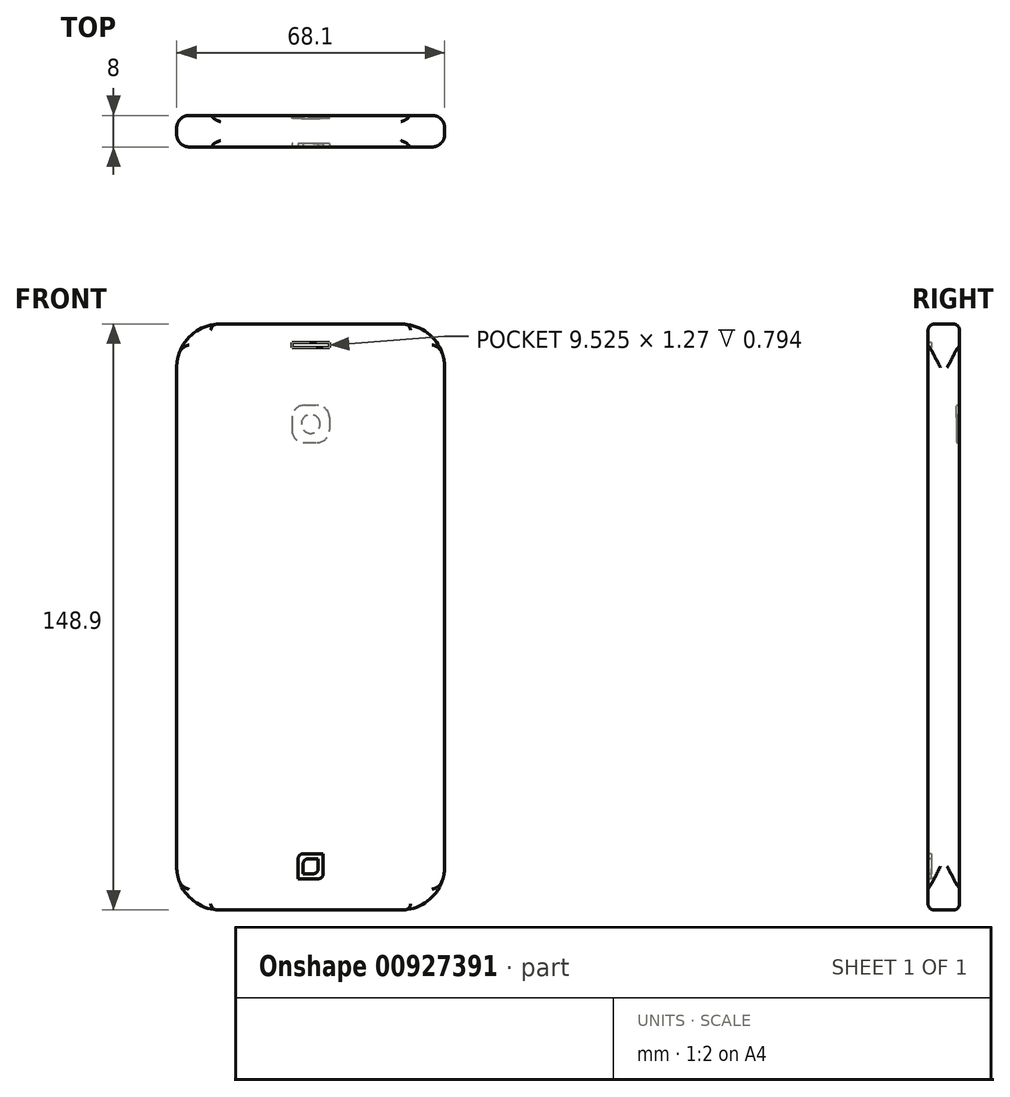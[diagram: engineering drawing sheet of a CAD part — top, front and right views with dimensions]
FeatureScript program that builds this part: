
annotation { "Feature Type Name" : "Feature", "Feature Type Description" : "" }
export const myFeature = defineFeature(function(context is Context, id is Id, definition is map)
    precondition{}
    {
        {
            var Q0;
            Q0=qCreatedBy(makeId("Front.planeOp"),FACE);
            var sketch = newSketch(context, id + "F0", { "sketchPlane" : qUnion([Q0])});
            skLineSegment(sketch, "E0.bottom", {"start": v(34.05, 74.45) * mm, "end": v(-34.05, 74.45) * mm});
            skLineSegment(sketch, "E0.top", {"start": v(34.05, -74.45) * mm, "end": v(-34.05, -74.45) * mm});
            skLineSegment(sketch, "E0.left", {"start": v(34.05, 74.45) * mm, "end": v(34.05, -74.45) * mm});
            skLineSegment(sketch, "E0.right", {"start": v(-34.05, 74.45) * mm, "end": v(-34.05, -74.45) * mm});
            skPoint(sketch, "E0.middle", {"position": v(0, 0) * mm});
            skSolve(sketch);
        }
        {
            var Q0;
            Q0 = qSketchRegion(id + "F0", true);
            extrude(context, id + "F1", {"entities" : qUnion([Q0]), "depth" : 8 * mm, "offsetDistance" : 25.4 * mm});
        }
        {
            var Q0;
            Q0=makeQuery(id+"F1.opExtrude","SWEPT_EDGE",EDGE,{"disambiguationData":[OSD([sQuery(id+"F0.wireOp",EDGE,"E0.bottom"),sQuery(id+"F0.wireOp",EDGE,"E0.left")])]});
            var Q1;
            Q1=makeQuery(id+"F1.opExtrude","SWEPT_EDGE",EDGE,{"disambiguationData":[OSD([sQuery(id+"F0.wireOp",EDGE,"E0.bottom"),sQuery(id+"F0.wireOp",EDGE,"E0.right")])]});
            var Q2;
            Q2=makeQuery(id+"F1.opExtrude","SWEPT_EDGE",EDGE,{"disambiguationData":[OSD([sQuery(id+"F0.wireOp",EDGE,"E0.top"),sQuery(id+"F0.wireOp",EDGE,"E0.right")])]});
            var Q3;
            Q3=makeQuery(id+"F1.opExtrude","SWEPT_EDGE",EDGE,{"disambiguationData":[OSD([sQuery(id+"F0.wireOp",EDGE,"E0.top"),sQuery(id+"F0.wireOp",EDGE,"E0.left")])]});
            fillet(context, id + "F2", {"entities" : qUnion([Q0, Q1, Q2, Q3]), "radius" : 11.1 * mm, "tangentPropagation" : true, "allowEdgeOverflow" : false});
        }
        {
            var Q0;
            Q0=makeQuery(id+"F1.opExtrude","CAP_FACE",FACE,{"disambiguationData":[OSD([sQuery(id+"F0.wireOp",EDGE,"E0.bottom"),sQuery(id+"F0.wireOp",EDGE,"E0.top"),sQuery(id+"F0.wireOp",EDGE,"E0.left"),sQuery(id+"F0.wireOp",EDGE,"E0.right")])],"isStart":true});
            var sketch = newSketch(context, id + "F3", { "sketchPlane" : qUnion([Q0])});
            skLineSegment(sketch, "E1.bottom", {"start": v(4.76, 53.81) * mm, "end": v(-4.76, 53.81) * mm});
            skLineSegment(sketch, "E1.top", {"start": v(4.76, 44.29) * mm, "end": v(-4.76, 44.29) * mm});
            skLineSegment(sketch, "E1.left", {"start": v(4.76, 53.81) * mm, "end": v(4.76, 44.29) * mm});
            skLineSegment(sketch, "E1.right", {"start": v(-4.76, 53.81) * mm, "end": v(-4.76, 44.29) * mm});
            skPoint(sketch, "E1.middle", {"position": v(0, 49.05) * mm});
            skCircle(sketch, "E2", {"center": v(0, 49.05) * mm, "radius": 2.38 * mm});
            skSolve(sketch);
        }
        {
            var Q0;
            Q0 = qSketchRegion(id + "F3", true);
            extrude(context, id + "F4", {"entities" : qUnion([Q0]), "operationType" : NewBodyOperationType.REMOVE, "oppositeDirection" : true, "depth" : 0.8 * mm, "offsetDistance" : 25.4 * mm});
        }
        {
            var Q0;
            Q0=makeQuery(id+"F1.opExtrude","CAP_EDGE",EDGE,{"disambiguationData":[OSD([sQuery(id+"F0.wireOp",EDGE,"E0.left")])],"isStart":false});
            var Q1;
            Q1=makeQuery(id+"F1.opExtrude","CAP_EDGE",EDGE,{"disambiguationData":[OSD([sQuery(id+"F0.wireOp",EDGE,"E0.right")])],"isStart":false});
            var Q2;
            Q2=makeQuery(id+"F1.opExtrude","CAP_EDGE",EDGE,{"disambiguationData":[OSD([sQuery(id+"F0.wireOp",EDGE,"E0.right")])],"isStart":true});
            var Q3;
            Q3=makeQuery(id+"F1.opExtrude","CAP_EDGE",EDGE,{"disambiguationData":[OSD([sQuery(id+"F0.wireOp",EDGE,"E0.left")])],"isStart":true});
            fillet(context, id + "F5", {"entities" : qUnion([Q0, Q1, Q2, Q3]), "radius" : 3.17 * mm, "allowEdgeOverflow" : false});
        }
        {
            var Q0;
            Q0=makeQuery(id+"F1.opExtrude","CAP_EDGE",EDGE,{"disambiguationData":[OSD([sQuery(id+"F0.wireOp",EDGE,"E0.top")])],"isStart":false});
            var Q1;
            Q1=makeQuery(id+"F1.opExtrude","CAP_EDGE",EDGE,{"disambiguationData":[OSD([sQuery(id+"F0.wireOp",EDGE,"E0.top")])],"isStart":true});
            var Q2;
            Q2=makeQuery(id+"F1.opExtrude","CAP_EDGE",EDGE,{"disambiguationData":[OSD([sQuery(id+"F0.wireOp",EDGE,"E0.bottom")])],"isStart":false});
            var Q3;
            Q3=makeQuery(id+"F1.opExtrude","CAP_EDGE",EDGE,{"disambiguationData":[OSD([sQuery(id+"F0.wireOp",EDGE,"E0.bottom")])],"isStart":true});
            fillet(context, id + "F6", {"entities" : qUnion([Q0, Q1, Q2, Q3]), "radius" : 1.59 * mm, "allowEdgeOverflow" : false});
        }
        {
            var Q0;
            {var subQ0=sQuery(id+"F0.wireOp",EDGE,"E0.right");var subQ1=sQuery(id+"F0.wireOp",EDGE,"E0.bottom");Q0=makeQuery(id+"F2.opFillet","BLEND_EDGE",EDGE,{"blendedFrom":[makeQuery(id+"F1.opExtrude","SWEPT_EDGE",EDGE,{"disambiguationData":[OSD([subQ1,subQ0])]}),makeQuery(id+"F1.opExtrude","CAP_FACE",FACE,{"disambiguationData":[OSD([subQ1,sQuery(id+"F0.wireOp",EDGE,"E0.top"),sQuery(id+"F0.wireOp",EDGE,"E0.left"),subQ0])],"isStart":false})],"blendedInto":[makeQuery(id+"F1.opExtrude","CAP_FACE",FACE,{"disambiguationData":[OSD([subQ1,sQuery(id+"F0.wireOp",EDGE,"E0.top"),sQuery(id+"F0.wireOp",EDGE,"E0.left"),subQ0])],"isStart":false})]});}
            var Q1;
            {var subQ0=sQuery(id+"F0.wireOp",EDGE,"E0.right");var subQ1=sQuery(id+"F0.wireOp",EDGE,"E0.bottom");Q1=makeQuery(id+"F2.opFillet","BLEND_EDGE",EDGE,{"blendedFrom":[makeQuery(id+"F1.opExtrude","SWEPT_EDGE",EDGE,{"disambiguationData":[OSD([subQ1,subQ0])]}),makeQuery(id+"F1.opExtrude","CAP_FACE",FACE,{"disambiguationData":[OSD([subQ1,sQuery(id+"F0.wireOp",EDGE,"E0.top"),sQuery(id+"F0.wireOp",EDGE,"E0.left"),subQ0])],"isStart":true})],"blendedInto":[makeQuery(id+"F1.opExtrude","CAP_FACE",FACE,{"disambiguationData":[OSD([subQ1,sQuery(id+"F0.wireOp",EDGE,"E0.top"),sQuery(id+"F0.wireOp",EDGE,"E0.left"),subQ0])],"isStart":true})]});}
            var Q2;
            {var subQ0=sQuery(id+"F0.wireOp",EDGE,"E0.left");var subQ1=sQuery(id+"F0.wireOp",EDGE,"E0.bottom");Q2=makeQuery(id+"F2.opFillet","BLEND_EDGE",EDGE,{"blendedFrom":[makeQuery(id+"F1.opExtrude","SWEPT_EDGE",EDGE,{"disambiguationData":[OSD([subQ1,subQ0])]}),makeQuery(id+"F1.opExtrude","CAP_FACE",FACE,{"disambiguationData":[OSD([subQ1,sQuery(id+"F0.wireOp",EDGE,"E0.top"),subQ0,sQuery(id+"F0.wireOp",EDGE,"E0.right")])],"isStart":false})],"blendedInto":[makeQuery(id+"F1.opExtrude","CAP_FACE",FACE,{"disambiguationData":[OSD([subQ1,sQuery(id+"F0.wireOp",EDGE,"E0.top"),subQ0,sQuery(id+"F0.wireOp",EDGE,"E0.right")])],"isStart":false})]});}
            var Q3;
            {var subQ0=sQuery(id+"F0.wireOp",EDGE,"E0.left");var subQ1=sQuery(id+"F0.wireOp",EDGE,"E0.bottom");Q3=makeQuery(id+"F2.opFillet","BLEND_EDGE",EDGE,{"blendedFrom":[makeQuery(id+"F1.opExtrude","SWEPT_EDGE",EDGE,{"disambiguationData":[OSD([subQ1,subQ0])]}),makeQuery(id+"F1.opExtrude","CAP_FACE",FACE,{"disambiguationData":[OSD([subQ1,sQuery(id+"F0.wireOp",EDGE,"E0.top"),subQ0,sQuery(id+"F0.wireOp",EDGE,"E0.right")])],"isStart":true})],"blendedInto":[makeQuery(id+"F1.opExtrude","CAP_FACE",FACE,{"disambiguationData":[OSD([subQ1,sQuery(id+"F0.wireOp",EDGE,"E0.top"),subQ0,sQuery(id+"F0.wireOp",EDGE,"E0.right")])],"isStart":true})]});}
            var Q4;
            {var subQ0=sQuery(id+"F0.wireOp",EDGE,"E0.left");var subQ1=sQuery(id+"F0.wireOp",EDGE,"E0.top");Q4=makeQuery(id+"F2.opFillet","BLEND_EDGE",EDGE,{"blendedFrom":[makeQuery(id+"F1.opExtrude","SWEPT_EDGE",EDGE,{"disambiguationData":[OSD([subQ1,subQ0])]}),makeQuery(id+"F1.opExtrude","CAP_FACE",FACE,{"disambiguationData":[OSD([sQuery(id+"F0.wireOp",EDGE,"E0.bottom"),subQ1,subQ0,sQuery(id+"F0.wireOp",EDGE,"E0.right")])],"isStart":true})],"blendedInto":[makeQuery(id+"F1.opExtrude","CAP_FACE",FACE,{"disambiguationData":[OSD([sQuery(id+"F0.wireOp",EDGE,"E0.bottom"),subQ1,subQ0,sQuery(id+"F0.wireOp",EDGE,"E0.right")])],"isStart":true})]});}
            var Q5;
            {var subQ0=sQuery(id+"F0.wireOp",EDGE,"E0.left");var subQ1=sQuery(id+"F0.wireOp",EDGE,"E0.top");Q5=makeQuery(id+"F2.opFillet","BLEND_EDGE",EDGE,{"blendedFrom":[makeQuery(id+"F1.opExtrude","SWEPT_EDGE",EDGE,{"disambiguationData":[OSD([subQ1,subQ0])]}),makeQuery(id+"F1.opExtrude","CAP_FACE",FACE,{"disambiguationData":[OSD([sQuery(id+"F0.wireOp",EDGE,"E0.bottom"),subQ1,subQ0,sQuery(id+"F0.wireOp",EDGE,"E0.right")])],"isStart":false})],"blendedInto":[makeQuery(id+"F1.opExtrude","CAP_FACE",FACE,{"disambiguationData":[OSD([sQuery(id+"F0.wireOp",EDGE,"E0.bottom"),subQ1,subQ0,sQuery(id+"F0.wireOp",EDGE,"E0.right")])],"isStart":false})]});}
            var Q6;
            {var subQ0=sQuery(id+"F0.wireOp",EDGE,"E0.right");var subQ1=sQuery(id+"F0.wireOp",EDGE,"E0.top");Q6=makeQuery(id+"F2.opFillet","BLEND_EDGE",EDGE,{"blendedFrom":[makeQuery(id+"F1.opExtrude","SWEPT_EDGE",EDGE,{"disambiguationData":[OSD([subQ1,subQ0])]}),makeQuery(id+"F1.opExtrude","CAP_FACE",FACE,{"disambiguationData":[OSD([sQuery(id+"F0.wireOp",EDGE,"E0.bottom"),subQ1,sQuery(id+"F0.wireOp",EDGE,"E0.left"),subQ0])],"isStart":true})],"blendedInto":[makeQuery(id+"F1.opExtrude","CAP_FACE",FACE,{"disambiguationData":[OSD([sQuery(id+"F0.wireOp",EDGE,"E0.bottom"),subQ1,sQuery(id+"F0.wireOp",EDGE,"E0.left"),subQ0])],"isStart":true})]});}
            var Q7;
            {var subQ0=sQuery(id+"F0.wireOp",EDGE,"E0.right");var subQ1=sQuery(id+"F0.wireOp",EDGE,"E0.top");Q7=makeQuery(id+"F2.opFillet","BLEND_EDGE",EDGE,{"blendedFrom":[makeQuery(id+"F1.opExtrude","SWEPT_EDGE",EDGE,{"disambiguationData":[OSD([subQ1,subQ0])]}),makeQuery(id+"F1.opExtrude","CAP_FACE",FACE,{"disambiguationData":[OSD([sQuery(id+"F0.wireOp",EDGE,"E0.bottom"),subQ1,sQuery(id+"F0.wireOp",EDGE,"E0.left"),subQ0])],"isStart":false})],"blendedInto":[makeQuery(id+"F1.opExtrude","CAP_FACE",FACE,{"disambiguationData":[OSD([sQuery(id+"F0.wireOp",EDGE,"E0.bottom"),subQ1,sQuery(id+"F0.wireOp",EDGE,"E0.left"),subQ0])],"isStart":false})]});}
            fillet(context, id + "F7", {"entities" : qUnion([Q0, Q1, Q2, Q3, Q4, Q5, Q6, Q7]), "radius" : 1.27 * mm, "allowEdgeOverflow" : false});
        }
        {
            var Q0;
            Q0=makeQuery(id+"F4.boolean.opBoolean","COPY",EDGE,{"derivedFrom":makeQuery(id+"F4.opExtrude","SWEPT_EDGE",EDGE,{"disambiguationData":[OSD([sQuery(id+"F3.wireOp",EDGE,"E1.bottom"),sQuery(id+"F3.wireOp",EDGE,"E1.right")])]})});
            var Q1;
            Q1=makeQuery(id+"F4.boolean.opBoolean","COPY",EDGE,{"derivedFrom":makeQuery(id+"F4.opExtrude","SWEPT_EDGE",EDGE,{"disambiguationData":[OSD([sQuery(id+"F3.wireOp",EDGE,"E1.bottom"),sQuery(id+"F3.wireOp",EDGE,"E1.left")])]})});
            var Q2;
            Q2=makeQuery(id+"F4.boolean.opBoolean","COPY",EDGE,{"derivedFrom":makeQuery(id+"F4.opExtrude","SWEPT_EDGE",EDGE,{"disambiguationData":[OSD([sQuery(id+"F3.wireOp",EDGE,"E1.top"),sQuery(id+"F3.wireOp",EDGE,"E1.left")])]})});
            var Q3;
            Q3=makeQuery(id+"F4.boolean.opBoolean","COPY",EDGE,{"derivedFrom":makeQuery(id+"F4.opExtrude","SWEPT_EDGE",EDGE,{"disambiguationData":[OSD([sQuery(id+"F3.wireOp",EDGE,"E1.top"),sQuery(id+"F3.wireOp",EDGE,"E1.right")])]})});
            fillet(context, id + "F8", {"entities" : qUnion([Q0, Q1, Q2, Q3]), "radius" : 3.17 * mm, "tangentPropagation" : true, "allowEdgeOverflow" : false});
        }
        {
            var Q0;
            Q0=makeQuery(id+"F1.opExtrude","CAP_FACE",FACE,{"disambiguationData":[OSD([sQuery(id+"F0.wireOp",EDGE,"E0.bottom"),sQuery(id+"F0.wireOp",EDGE,"E0.top"),sQuery(id+"F0.wireOp",EDGE,"E0.left"),sQuery(id+"F0.wireOp",EDGE,"E0.right")])],"isStart":false});
            var sketch = newSketch(context, id + "F9", { "sketchPlane" : qUnion([Q0])});
            skLineSegment(sketch, "E3.bottom", {"start": v(3.18, -60.16) * mm, "end": v(-3.18, -60.16) * mm});
            skLineSegment(sketch, "E3.top", {"start": v(3.17, -66.51) * mm, "end": v(-3.18, -66.51) * mm});
            skLineSegment(sketch, "E3.left", {"start": v(3.18, -60.16) * mm, "end": v(3.18, -66.51) * mm});
            skLineSegment(sketch, "E3.right", {"start": v(-3.17, -60.16) * mm, "end": v(-3.17, -66.51) * mm});
            skPoint(sketch, "E3.middle", {"position": v(0, -63.34) * mm});
            skLineSegment(sketch, "E4.bottom", {"start": v(1.9, -61.43) * mm, "end": v(-1.9, -61.43) * mm});
            skLineSegment(sketch, "E4.top", {"start": v(1.9, -65.24) * mm, "end": v(-1.9, -65.24) * mm});
            skLineSegment(sketch, "E4.left", {"start": v(1.9, -61.43) * mm, "end": v(1.9, -65.24) * mm});
            skLineSegment(sketch, "E4.right", {"start": v(-1.9, -61.43) * mm, "end": v(-1.9, -65.24) * mm});
            skLineSegment(sketch, "E5.bottom", {"start": v(4.76, 69.69) * mm, "end": v(-4.76, 69.69) * mm});
            skLineSegment(sketch, "E5.top", {"start": v(4.76, 68.42) * mm, "end": v(-4.76, 68.42) * mm});
            skLineSegment(sketch, "E5.left", {"start": v(4.76, 69.69) * mm, "end": v(4.76, 68.42) * mm});
            skLineSegment(sketch, "E5.right", {"start": v(-4.76, 69.69) * mm, "end": v(-4.76, 68.42) * mm});
            skPoint(sketch, "E5.middle", {"position": v(0, 69.05) * mm});
            skSolve(sketch);
        }
        {
            var Q0;
            Q0 = qSketchRegion(id + "F9", true);
            extrude(context, id + "F10", {"entities" : qUnion([Q0]), "operationType" : NewBodyOperationType.REMOVE, "oppositeDirection" : true, "depth" : 0.8 * mm, "offsetDistance" : 25.4 * mm});
        }
        {
            var Q0;
            Q0=makeQuery(id+"F10.boolean.opBoolean","COPY",EDGE,{"derivedFrom":makeQuery(id+"F10.opExtrude","SWEPT_EDGE",EDGE,{"disambiguationData":[OSD([sQuery(id+"F9.wireOp",EDGE,"E3.bottom"),sQuery(id+"F9.wireOp",EDGE,"E3.right")])]})});
            var Q1;
            Q1=makeQuery(id+"F10.boolean.opBoolean","COPY",EDGE,{"derivedFrom":makeQuery(id+"F10.opExtrude","SWEPT_EDGE",EDGE,{"disambiguationData":[OSD([sQuery(id+"F9.wireOp",EDGE,"E4.bottom"),sQuery(id+"F9.wireOp",EDGE,"E4.right")])]})});
            var Q2;
            Q2=makeQuery(id+"F10.boolean.opBoolean","COPY",EDGE,{"derivedFrom":makeQuery(id+"F10.opExtrude","SWEPT_EDGE",EDGE,{"disambiguationData":[OSD([sQuery(id+"F9.wireOp",EDGE,"E3.top"),sQuery(id+"F9.wireOp",EDGE,"E3.left")])]})});
            var Q3;
            Q3=makeQuery(id+"F10.boolean.opBoolean","COPY",EDGE,{"derivedFrom":makeQuery(id+"F10.opExtrude","SWEPT_EDGE",EDGE,{"disambiguationData":[OSD([sQuery(id+"F9.wireOp",EDGE,"E4.top"),sQuery(id+"F9.wireOp",EDGE,"E4.left")])]})});
            fillet(context, id + "F11", {"entities" : qUnion([Q0, Q1, Q2, Q3]), "radius" : 1.27 * mm, "tangentPropagation" : true, "allowEdgeOverflow" : false});
        }
    });
